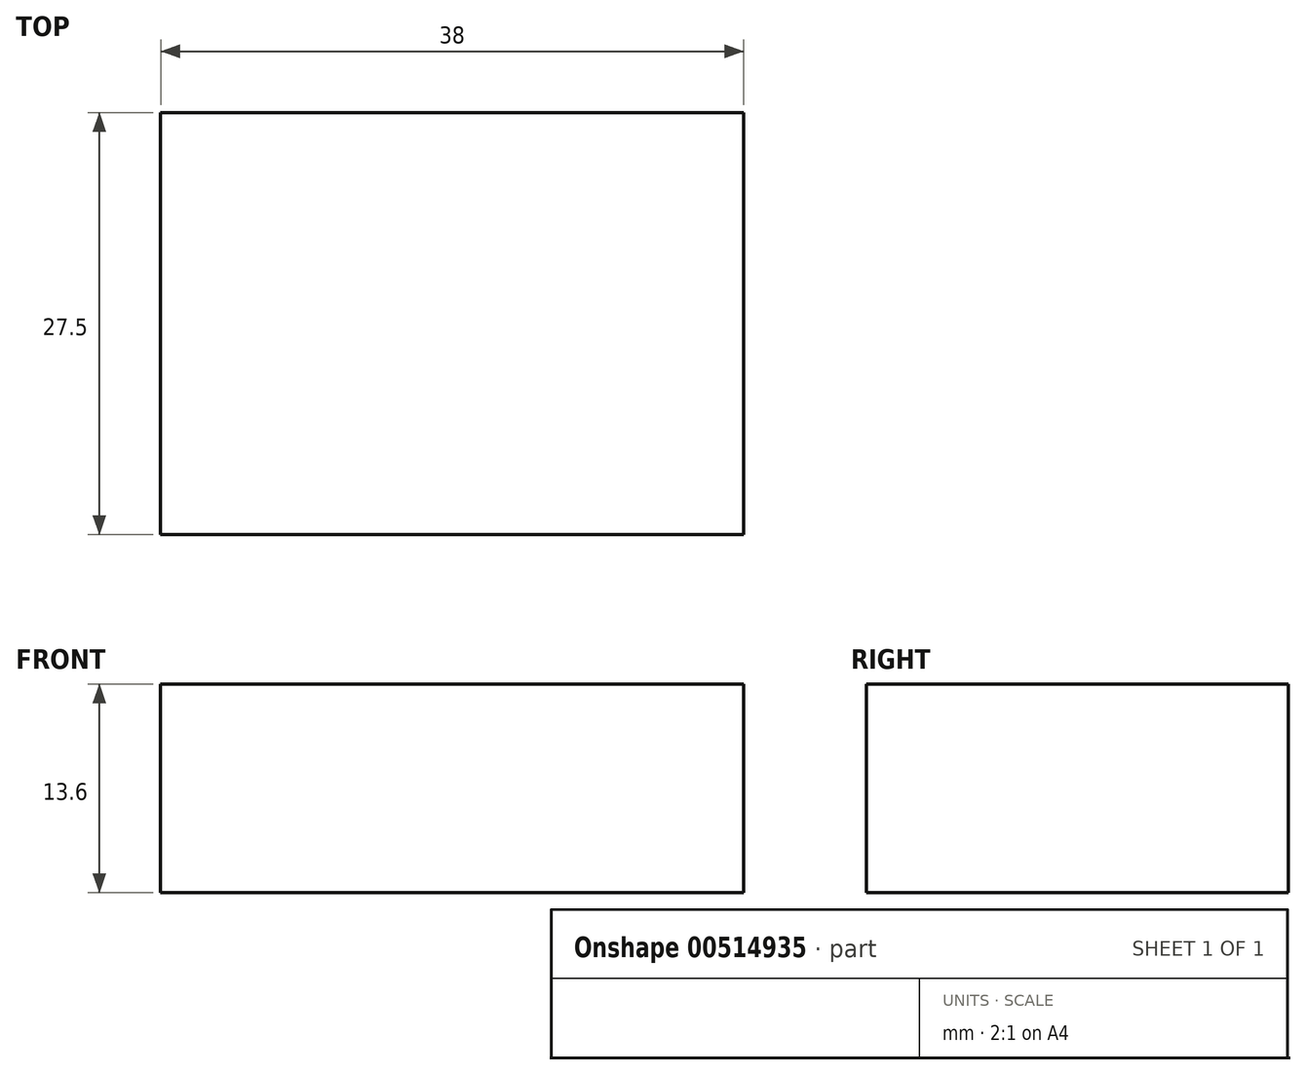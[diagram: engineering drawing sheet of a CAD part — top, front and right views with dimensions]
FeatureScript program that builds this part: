
annotation { "Feature Type Name" : "Feature", "Feature Type Description" : "" }
export const myFeature = defineFeature(function(context is Context, id is Id, definition is map)
    precondition{}
    {
        {
            var Q0;
            Q0=qCreatedBy(makeId("Top.planeOp"),FACE);
            var sketch = newSketch(context, id + "F0", { "sketchPlane" : qUnion([Q0])});
            skLineSegment(sketch, "E0.bottom", {"start": v(-18.11, 15.57) * mm, "end": v(19.89, 15.57) * mm});
            skLineSegment(sketch, "E0.top", {"start": v(-18.11, -11.93) * mm, "end": v(19.89, -11.93) * mm});
            skLineSegment(sketch, "E0.left", {"start": v(-18.11, 15.57) * mm, "end": v(-18.11, -11.93) * mm});
            skLineSegment(sketch, "E0.right", {"start": v(19.89, 15.57) * mm, "end": v(19.89, -11.93) * mm});
            skSolve(sketch);
        }
        {
            var Q0;
            Q0 = qSketchRegion(id + "F0", true);
            extrude(context, id + "F1", {"entities" : qUnion([Q0]), "depth" : 13.6 * mm, "offsetDistance" : 25 * mm});
        }
    });
